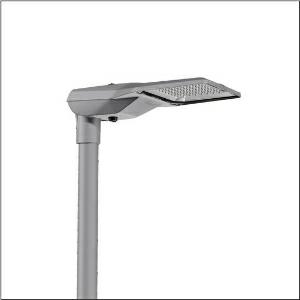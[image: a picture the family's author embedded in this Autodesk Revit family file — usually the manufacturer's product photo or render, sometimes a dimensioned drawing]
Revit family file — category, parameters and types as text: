
# Revit family: streetlight_sl_21_iq_midi___pl52_5xe3h31y08mb_cc6d
name_source: partatom
category: Lighting Fixtures
units: mm (PartAtom-declared; Revit-internal decimal feet)

## family parameters
Cut with Voids When Loaded = No
Host = Face
Light Source = No
Part Type = Normal
Room Calculation Point = No
Round Connector Dimension = Use Diameter
Shared = No

## types (1)
- --- (1 x LED, 18020 lm, 129.3 W, 3000K)
    Apparent Load = 129 VA
    CIE Flux Codes = 27 59 98 100 100
    Color Rendering = 70
    Color Temperature = 3000K
    Default Elevation = 1800 mm
    Description = Streetlight SL 21 iQ midi, mast luminaire, primary light control with lens, of PMMA, primary optical cover: cover, of toughened safety glass, transparent, light distribution: PL52, light emission: direct distribution, primary light characteristic: asymmetric, installation type: post-top, side-entry, LED, High Power LED, rated luminous flux: 18.020lm, luminous efficacy: 139lm/W, light colour: 730, colour temperature: 3000K, control gear: iQ-Street Remote, D4i with power reduction, control: pre-setting: logarithmic dimming characteristic, Street-Remote, Auto-Match, Temp-Guard, Lumen-Switch, Night-Set, Smart-Wire, Light-Fading, Desk-Remote (wireless, voltage-free reading and setting of iQ features in the workshop via application-optimized NFC function/RFID function), optimised constant luminous flux control (CLO 2.0), mains connection: 230..240V, AC, 50/60Hz, start of lifetime: 129W, end of service life: 142W, reduction: 56W, luminaire housing, of diecast aluminium, powder-coated, Siteco® metallic grey (DB 702S), corrosivity category C5 mid according to DIN EN ISO 12944, please order mast flange separately, inclination adjustable: 0°, 5°, 10°, 15°, sealing non-destructively replaceable, multi-level sealing system, length: 644mm, width: 335mm, height: 110mm, mast flange for spigot size: 42mm (side-entry): 5XC10008XM4, 60/48mm (side-entry/post-top): 5XC10108XM2, 76/60mm (side-entry/post-top): 5XC10108XM1, mounting height: 4..8m, Smart Interface below and above, protection rating (complete): IP66, insulation class (complete): insulation class II (safety insulation), certification: CE, ENEC, ENEC+, VDE, impact resistance: IK10, permissible operating ambient temperature for outdoor applications: -40..+50°C, standard-compliant lighting for roads and squares, packaging unit: 1 piece

Light Distribution: PL52
    Height = 111 mm
    Lamp = 1 x LED
    Lamp Light Flux = 18020 lm
    Lamp Power = 129.3 W
    Lamp count = 1
    Length = 644 mm
    Luminous efficacy = 139 lm/W
    Manufacturer = Siteco
    ModVariant = No
    Model = 5XE3H31Y08MB
    Number of Poles = 1
    OnlyDefault = Yes
    Power Factor = 1
    Product Name = Streetlight SL 21 iQ midi | PL52
    Product group = mast luminaire | pylon top
    ProductGroupID = 6100
    Protection Class = Protection class II
    Protection Degree = IP 66
    RLX_Detail_Level = 1
    RLX_Emergency_Light_Flux = 0 lm
    RLX_Emergency_Type = 0
    RLX_Emergency_Type_DB = No
    RlxData = <blob elided: 100641 chars, md5=c60498e9>
    Socket = socket
    Standby Power = 0 W
    System Light Flux = 18021 lm
    System Power = 129 W
    Type Comments = factory setting: luminous flux: 100 % | dim-lin: 254 | 672 mA
    Type Image = l_1004304.jpg
    URL = http://relux.com
    VarID = @adj_137351
    Voltage = 0 V
    Weight = 0.00 kg
    Width = 336 mm

## geometry (parser evidence)
native form markers: Blend x4, Sweep x11
no freeform markers — native parametric forms only
